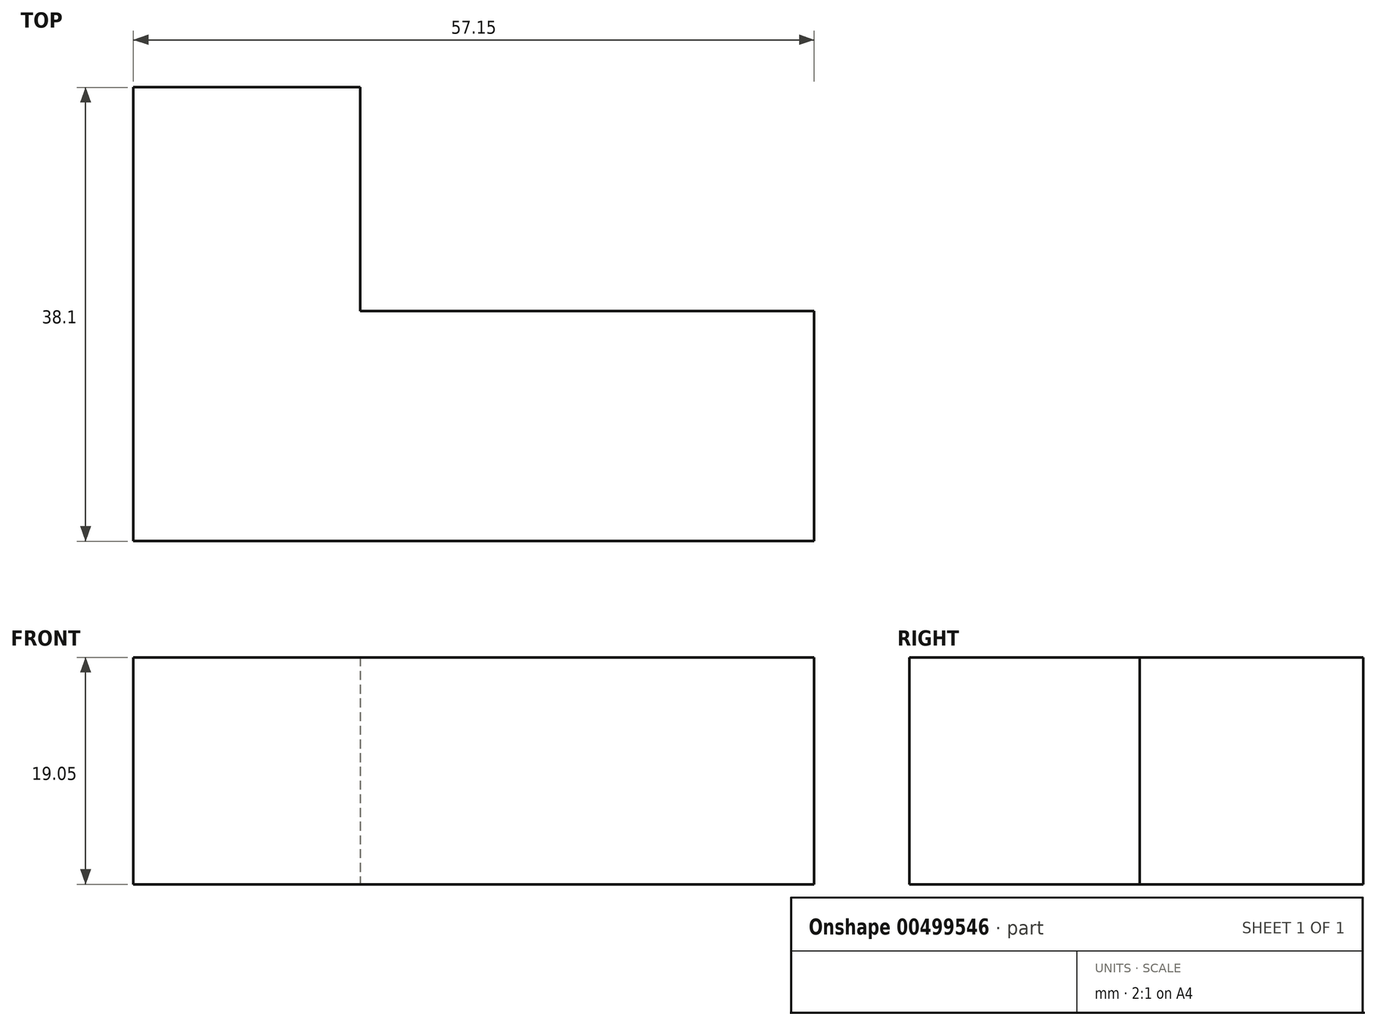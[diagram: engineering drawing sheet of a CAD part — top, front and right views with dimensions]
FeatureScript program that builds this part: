
annotation { "Feature Type Name" : "Feature", "Feature Type Description" : "" }
export const myFeature = defineFeature(function(context is Context, id is Id, definition is map)
    precondition{}
    {
        {
            var Q0;
            Q0=qCreatedBy(makeId("Top.planeOp"),FACE);
            var sketch = newSketch(context, id + "F0", { "sketchPlane" : qUnion([Q0])});
            skLineSegment(sketch, "E0.bottom", {"start": v(0, 0) * mm, "end": v(-19.05, 0) * mm});
            skLineSegment(sketch, "E0.top", {"start": v(0, 18.78) * mm, "end": v(-19.05, 18.78) * mm});
            skLineSegment(sketch, "E0.left", {"start": v(0, 0) * mm, "end": v(0, 18.78) * mm});
            skLineSegment(sketch, "E0.right", {"start": v(-19.05, 0) * mm, "end": v(-19.05, 18.78) * mm});
            skLineSegment(sketch, "E1.bottom", {"start": v(-19.05, 18.78) * mm, "end": v(0, 18.78) * mm});
            skLineSegment(sketch, "E1.top", {"start": v(-19.05, -19.32) * mm, "end": v(0, -19.32) * mm});
            skLineSegment(sketch, "E1.left", {"start": v(-19.05, 18.78) * mm, "end": v(-19.05, -19.32) * mm});
            skLineSegment(sketch, "E1.right", {"start": v(0, 18.78) * mm, "end": v(0, -19.32) * mm});
            skLineSegment(sketch, "E2.bottom", {"start": v(0, -19.32) * mm, "end": v(38.1, -19.32) * mm});
            skLineSegment(sketch, "E2.top", {"start": v(0, 0) * mm, "end": v(38.1, 0) * mm});
            skLineSegment(sketch, "E2.left", {"start": v(0, -19.32) * mm, "end": v(0, 0) * mm});
            skLineSegment(sketch, "E2.right", {"start": v(38.1, -19.32) * mm, "end": v(38.1, 0) * mm});
            skSolve(sketch);
        }
        {
            var Q0;
            Q0 = qSketchRegion(id + "F0", true);
            extrude(context, id + "F1", {"entities" : qUnion([Q0]), "depth" : 19.05 * mm});
        }
    });
